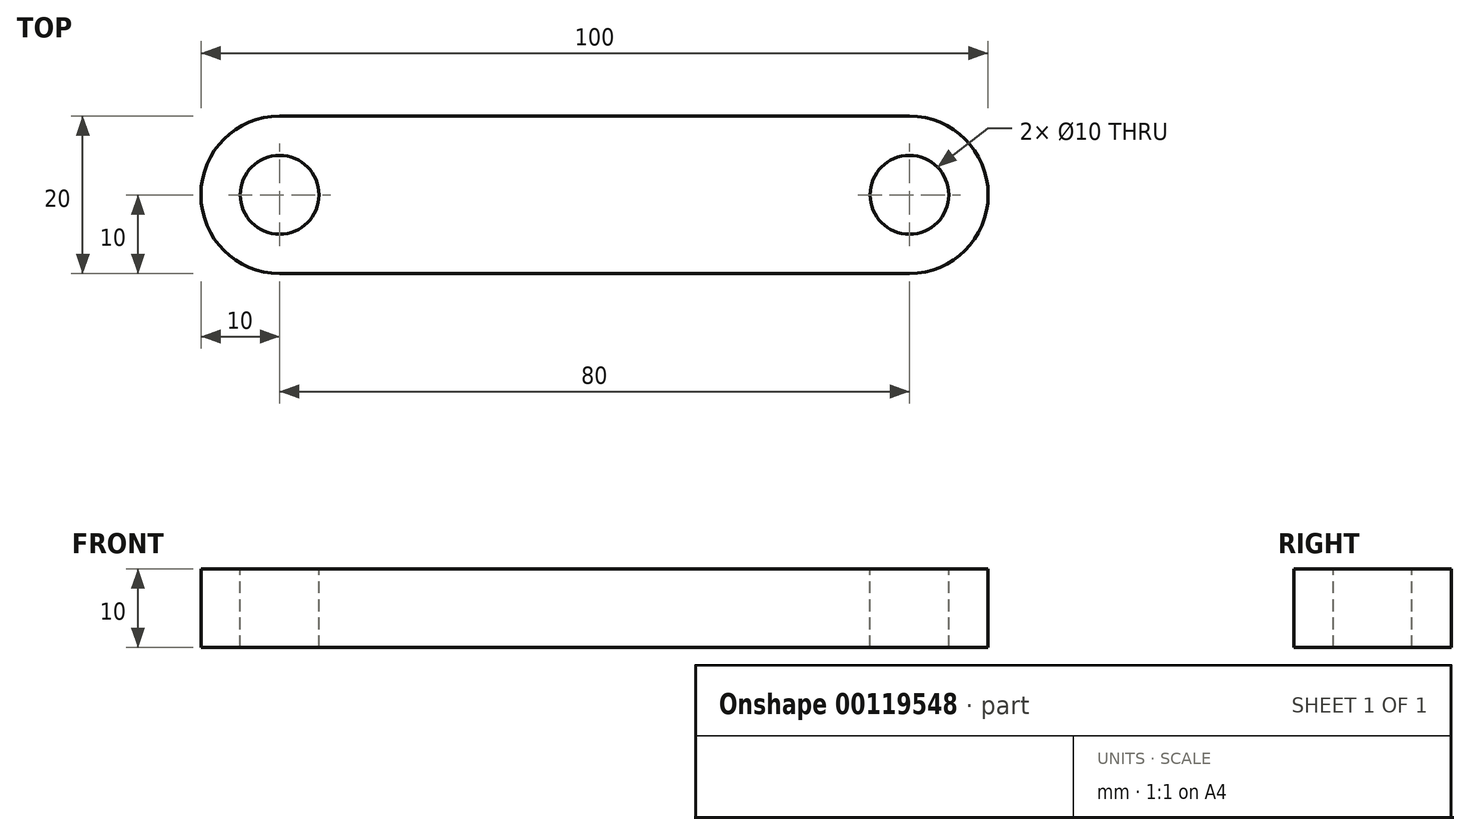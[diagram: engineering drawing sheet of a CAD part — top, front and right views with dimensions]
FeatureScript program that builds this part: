
annotation { "Feature Type Name" : "Feature", "Feature Type Description" : "" }
export const myFeature = defineFeature(function(context is Context, id is Id, definition is map)
    precondition{}
    {
        {
            var Q0;
            Q0=qCreatedBy(makeId("Top.planeOp"),FACE);
            var sketch = newSketch(context, id + "F0", { "sketchPlane" : qUnion([Q0])});
            skLineSegment(sketch, "E0", {"start": v(0, 0) * mm, "end": v(80, 0) * mm});
            skLineSegment(sketch, "E1", {"start": v(0, 20) * mm, "end": v(80, 20) * mm});
            skArc(sketch, "E2", {"start": v(0, 20) * mm, "mid": v(-10, 10) * mm, "end": v(0, 0) * mm});
            skArc(sketch, "E3", {"start": v(80, 0) * mm, "mid": v(90, 10) * mm, "end": v(80, 20) * mm});
            skSolve(sketch);
        }
        {
            var Q0;
            Q0 = qSketchRegion(id + "F0", true);
            extrude(context, id + "F1", {"entities" : qUnion([Q0]), "depth" : 10 * mm});
        }
        {
            var Q0;
            Q0=makeQuery(id+"F1.opExtrude","CAP_FACE",FACE,{"disambiguationData":[OSD([sQuery(id+"F0.wireOp",EDGE,"E0"),sQuery(id+"F0.wireOp",EDGE,"E1"),sQuery(id+"F0.wireOp",EDGE,"E2"),sQuery(id+"F0.wireOp",EDGE,"E3")])],"isStart":false});
            var sketch = newSketch(context, id + "F2", { "sketchPlane" : qUnion([Q0])});
            skLineSegment(sketch, "E4", {"start": v(0, 20) * mm, "end": v(0, 0) * mm, "construction": true});
            skLineSegment(sketch, "E5", {"start": v(80, 20) * mm, "end": v(80, 0) * mm, "construction": true});
            skCircle(sketch, "E6", {"center": v(0, 10) * mm, "radius": 5 * mm});
            skCircle(sketch, "E7", {"center": v(80, 10) * mm, "radius": 5 * mm});
            skSolve(sketch);
        }
        {
            var Q0;
            Q0 = qSketchRegion(id + "F2", true);
            extrude(context, id + "F3", {"entities" : qUnion([Q0]), "operationType" : NewBodyOperationType.REMOVE, "endBound" : BoundingType.THROUGH_ALL, "oppositeDirection" : true, "depth" : 25 * mm});
        }
    });
